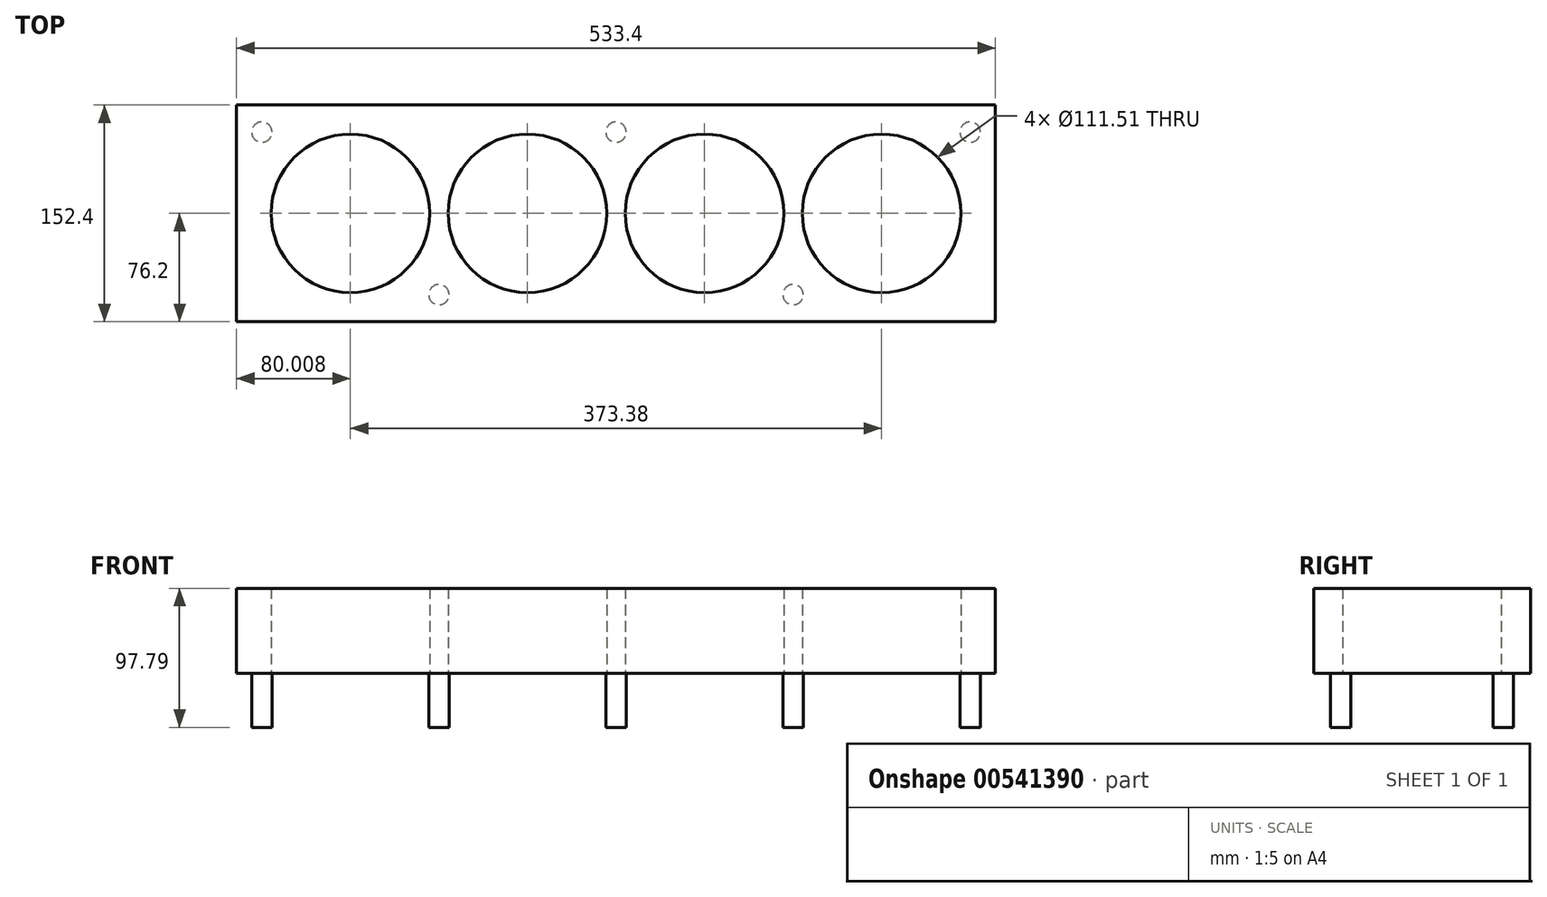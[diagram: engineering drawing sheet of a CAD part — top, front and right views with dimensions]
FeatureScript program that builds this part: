
annotation { "Feature Type Name" : "Feature", "Feature Type Description" : "" }
export const myFeature = defineFeature(function(context is Context, id is Id, definition is map)
    precondition{}
    {
        {
            var Q0;
            Q0=qCreatedBy(makeId("Top.planeOp"),FACE);
            var sketch = newSketch(context, id + "F0", { "sketchPlane" : qUnion([Q0])});
            skCircle(sketch, "E0", {"center": v(-145.84, 0) * mm, "radius": 55.75 * mm});
            skCircle(sketch, "E1.1.0.0", {"center": v(-21.38, 0) * mm, "radius": 55.75 * mm});
            skCircle(sketch, "E1.2.0.0", {"center": v(103.08, 0) * mm, "radius": 55.75 * mm});
            skCircle(sketch, "E1.3.0.0", {"center": v(227.54, 0) * mm, "radius": 55.75 * mm});
            skLineSegment(sketch, "E1.direction1", {"start": v(-145.84, 0) * mm, "end": v(-21.38, 0) * mm, "construction": true});
            skLineSegment(sketch, "E2", {"start": v(-145.84, 0) * mm, "end": v(227.54, 0) * mm, "construction": true});
            skLineSegment(sketch, "E3.bottom", {"start": v(307.55, 76.2) * mm, "end": v(-225.85, 76.2) * mm});
            skLineSegment(sketch, "E3.top", {"start": v(307.55, -76.2) * mm, "end": v(-225.85, -76.2) * mm});
            skLineSegment(sketch, "E3.left", {"start": v(307.55, 76.2) * mm, "end": v(307.55, -76.2) * mm});
            skLineSegment(sketch, "E3.right", {"start": v(-225.85, 76.2) * mm, "end": v(-225.85, -76.2) * mm});
            skPoint(sketch, "E3.middle", {"position": v(40.85, 0) * mm});
            skSolve(sketch);
        }
        {
            var Q0;
            Q0=makeQuery(id+"F0.imprint","IMPRINT",FACE,{"disambiguationData":[TD([[makeQuery(id+"F0.imprint","IMPRINT",EDGE,{"derivedFrom":sQuery(id+"F0.wireOp",EDGE,"E0")}),-1.0]])]});
            extrude(context, id + "F1", {"entities" : qUnion([Q0]), "depth" : 97.8 * mm, "offsetDistance" : 25.4 * mm});
        }
        {
            var Q0;
            Q0=makeQuery(id+"F1.opExtrude","CAP_FACE",FACE,{"disambiguationData":[OSD([sQuery(id+"F0.wireOp",EDGE,"E0"),sQuery(id+"F0.wireOp",EDGE,"E1.1.0.0"),sQuery(id+"F0.wireOp",EDGE,"E1.2.0.0"),sQuery(id+"F0.wireOp",EDGE,"E1.3.0.0"),sQuery(id+"F0.wireOp",EDGE,"E3.bottom"),sQuery(id+"F0.wireOp",EDGE,"E3.top"),sQuery(id+"F0.wireOp",EDGE,"E3.left"),sQuery(id+"F0.wireOp",EDGE,"E3.right")])],"isStart":true});
            var sketch = newSketch(context, id + "F2", { "sketchPlane" : qUnion([Q0])});
            skLineSegment(sketch, "E4", {"start": v(-145.84, 0) * mm, "end": v(-21.38, 0) * mm, "construction": true});
            skLineSegment(sketch, "E5", {"start": v(-83.61, 0) * mm, "end": v(-83.61, 57.15) * mm, "construction": true});
            skLineSegment(sketch, "E6", {"start": v(-21.38, 0) * mm, "end": v(103.08, 0) * mm, "construction": true});
            skLineSegment(sketch, "E7", {"start": v(103.08, 0) * mm, "end": v(227.54, 0) * mm, "construction": true});
            skLineSegment(sketch, "E8.MirrorCS", {"start": v(-83.61, 0) * mm, "end": v(-83.61, -57.15) * mm, "construction": true});
            skLineSegment(sketch, "E9", {"start": v(-21.38, 0) * mm, "end": v(-21.38, 20.7) * mm, "construction": true});
            skLineSegment(sketch, "E10", {"start": v(103.08, 0) * mm, "end": v(103.08, 22.94) * mm, "construction": true});
            skLineSegment(sketch, "E11", {"start": v(227.54, 0) * mm, "end": v(227.54, 18.08) * mm, "construction": true});
            skLineSegment(sketch, "E12.MirrorCS", {"start": v(40.85, 0) * mm, "end": v(40.85, 57.15) * mm, "construction": true});
            skLineSegment(sketch, "E13.MirrorCS", {"start": v(40.85, 0) * mm, "end": v(40.85, -57.15) * mm, "construction": true});
            skLineSegment(sketch, "E14.MirrorCS", {"start": v(165.3, 0) * mm, "end": v(165.3, 57.15) * mm, "construction": true});
            skLineSegment(sketch, "E15.MirrorCS", {"start": v(165.3, 0) * mm, "end": v(165.3, -57.15) * mm, "construction": true});
            skLineSegment(sketch, "E16.MirrorCS", {"start": v(289.77, 0) * mm, "end": v(289.77, 57.15) * mm, "construction": true});
            skLineSegment(sketch, "E17.MirrorCS", {"start": v(289.77, 0) * mm, "end": v(289.77, -57.15) * mm, "construction": true});
            skLineSegment(sketch, "E18", {"start": v(-145.84, 0) * mm, "end": v(-145.84, 30.4) * mm, "construction": true});
            skLineSegment(sketch, "E19.MirrorCS", {"start": v(-208.07, 0) * mm, "end": v(-208.07, 57.15) * mm, "construction": true});
            skLineSegment(sketch, "E20.MirrorCS", {"start": v(-208.07, 0) * mm, "end": v(-208.07, -57.15) * mm, "construction": true});
            skCircle(sketch, "E21", {"center": v(-208.07, 57.15) * mm, "radius": 7.14 * mm});
            skCircle(sketch, "E22.MirrorC", {"center": v(-208.07, -57.15) * mm, "radius": 7.14 * mm});
            skCircle(sketch, "E23.MirrorC", {"center": v(-83.61, 57.15) * mm, "radius": 7.14 * mm});
            skCircle(sketch, "E24.MirrorC", {"center": v(-83.61, -57.15) * mm, "radius": 7.14 * mm});
            skCircle(sketch, "E25.MirrorC", {"center": v(40.85, 57.15) * mm, "radius": 7.14 * mm});
            skCircle(sketch, "E26.MirrorC", {"center": v(40.85, -57.15) * mm, "radius": 7.14 * mm});
            skCircle(sketch, "E27.MirrorC", {"center": v(165.3, 57.15) * mm, "radius": 7.14 * mm});
            skCircle(sketch, "E28.MirrorC", {"center": v(165.3, -57.15) * mm, "radius": 7.14 * mm});
            skCircle(sketch, "E29.MirrorC", {"center": v(289.77, 57.15) * mm, "radius": 7.14 * mm});
            skCircle(sketch, "E30.MirrorC", {"center": v(289.77, -57.15) * mm, "radius": 7.14 * mm});
            skSolve(sketch);
        }
        {
            var Q0;
            Q0=makeQuery(id+"F2.imprint","IMPRINT",FACE,{"disambiguationData":[TD([[makeQuery(id+"F2.imprint","IMPRINT",EDGE,{"derivedFrom":sQuery(id+"F2.wireOp",EDGE,"E21")}),1.0]])]});
            var Q1;
            Q1=makeQuery(id+"F2.imprint","IMPRINT",FACE,{"disambiguationData":[TD([[makeQuery(id+"F2.imprint","IMPRINT",EDGE,{"derivedFrom":sQuery(id+"F2.wireOp",EDGE,"E23.MirrorC")}),-1.0]])]});
            var Q2;
            Q2=makeQuery(id+"F2.imprint","IMPRINT",FACE,{"disambiguationData":[TD([[makeQuery(id+"F2.imprint","IMPRINT",EDGE,{"derivedFrom":sQuery(id+"F2.wireOp",EDGE,"E22.MirrorC")}),-1.0]])]});
            var Q3;
            Q3=makeQuery(id+"F2.imprint","IMPRINT",FACE,{"disambiguationData":[TD([[makeQuery(id+"F2.imprint","IMPRINT",EDGE,{"derivedFrom":sQuery(id+"F2.wireOp",EDGE,"E24.MirrorC")}),1.0]])]});
            var Q4;
            Q4=makeQuery(id+"F2.imprint","IMPRINT",FACE,{"disambiguationData":[TD([[makeQuery(id+"F2.imprint","IMPRINT",EDGE,{"derivedFrom":sQuery(id+"F2.wireOp",EDGE,"E25.MirrorC")}),1.0]])]});
            var Q5;
            Q5=makeQuery(id+"F2.imprint","IMPRINT",FACE,{"disambiguationData":[TD([[makeQuery(id+"F2.imprint","IMPRINT",EDGE,{"derivedFrom":sQuery(id+"F2.wireOp",EDGE,"E26.MirrorC")}),-1.0]])]});
            var Q6;
            Q6=makeQuery(id+"F2.imprint","IMPRINT",FACE,{"disambiguationData":[TD([[makeQuery(id+"F2.imprint","IMPRINT",EDGE,{"derivedFrom":sQuery(id+"F2.wireOp",EDGE,"E28.MirrorC")}),1.0]])]});
            var Q7;
            Q7=makeQuery(id+"F2.imprint","IMPRINT",FACE,{"disambiguationData":[TD([[makeQuery(id+"F2.imprint","IMPRINT",EDGE,{"derivedFrom":sQuery(id+"F2.wireOp",EDGE,"E27.MirrorC")}),-1.0]])]});
            var Q8;
            Q8=makeQuery(id+"F2.imprint","IMPRINT",FACE,{"disambiguationData":[TD([[makeQuery(id+"F2.imprint","IMPRINT",EDGE,{"derivedFrom":sQuery(id+"F2.wireOp",EDGE,"E29.MirrorC")}),1.0]])]});
            var Q9;
            Q9=makeQuery(id+"F2.imprint","IMPRINT",FACE,{"disambiguationData":[TD([[makeQuery(id+"F2.imprint","IMPRINT",EDGE,{"derivedFrom":sQuery(id+"F2.wireOp",EDGE,"E30.MirrorC")}),-1.0]])]});
            extrude(context, id + "F3", {"entities" : qUnion([Q0, Q1, Q2, Q3, Q4, Q5, Q6, Q7, Q8, Q9]), "operationType" : NewBodyOperationType.REMOVE, "oppositeDirection" : true, "depth" : 38.1 * mm, "offsetDistance" : 25.4 * mm});
        }
    });
